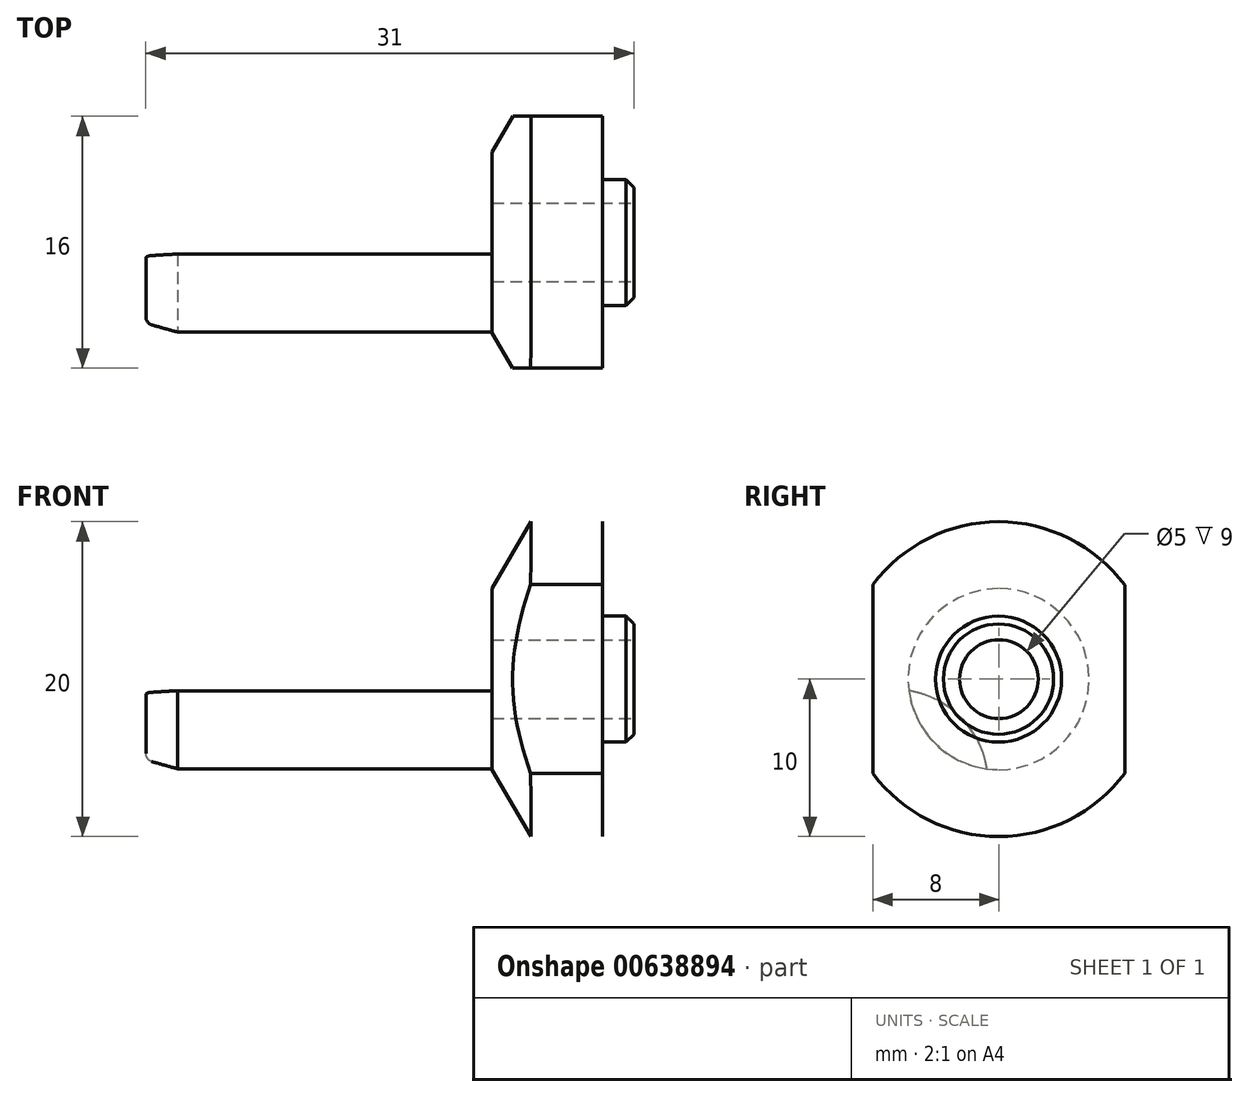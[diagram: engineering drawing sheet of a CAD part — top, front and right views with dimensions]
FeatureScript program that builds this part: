
annotation { "Feature Type Name" : "Feature", "Feature Type Description" : "" }
export const myFeature = defineFeature(function(context is Context, id is Id, definition is map)
    precondition{}
    {
        {
            var Q0;
            Q0=qCreatedBy(makeId("Top.planeOp"),FACE);
            var sketch = newSketch(context, id + "F0", { "sketchPlane" : qUnion([Q0])});
            skEllipticalArc(sketch, "E0", {});
            skEllipticalArc(sketch, "E1", {});
            skLineSegment(sketch, "E2", {"start": v(33.77, -5.77) * mm, "end": v(33.77, 5.73) * mm});
            skLineSegment(sketch, "E3", {"start": v(13.77, 5.73) * mm, "end": v(33.77, 5.73) * mm});
            skLineSegment(sketch, "E4", {"start": v(33.77, 5.68) * mm, "end": v(13.59, 5.68) * mm});
            skLineSegment(sketch, "E5", {"start": v(13.77, -5.77) * mm, "end": v(33.77, -5.77) * mm});
            skLineSegment(sketch, "E6", {"start": v(33.77, -5.72) * mm, "end": v(13.59, -5.72) * mm});
            skLineSegment(sketch, "E7", {"start": v(33.77, 0.73) * mm, "end": v(13.77, 0.73) * mm});
            skLineSegment(sketch, "E8", {"start": v(33.77, -0.77) * mm, "end": v(13.77, -0.77) * mm});
            skLineSegment(sketch, "E9", {"start": v(42.27, 3.98) * mm, "end": v(42.27, -4.02) * mm});
            skLineSegment(sketch, "E10", {"start": v(42.77, 3.48) * mm, "end": v(42.27, 3.98) * mm});
            skLineSegment(sketch, "E11", {"start": v(42.27, -4.02) * mm, "end": v(42.77, -3.52) * mm});
            skLineSegment(sketch, "E12", {"start": v(40.77, 5.98) * mm, "end": v(36.23, -6.02) * mm});
            skLineSegment(sketch, "E13", {"start": v(40.77, -6.02) * mm, "end": v(36.23, 5.98) * mm});
            skLineSegment(sketch, "E14", {"start": v(36.23, 9.98) * mm, "end": v(36.23, 5.98) * mm});
            skLineSegment(sketch, "E15", {"start": v(36.23, -6.02) * mm, "end": v(36.23, -10.02) * mm});
            skEllipticalArc(sketch, "E16", {});
            skLineSegment(sketch, "E17", {"start": v(40.77, -6.02) * mm, "end": v(36.23, -6.02) * mm});
            skLineSegment(sketch, "E18", {"start": v(40.77, 5.98) * mm, "end": v(36.23, 5.98) * mm});
            skLineSegment(sketch, "E19", {"start": v(42.77, 3.48) * mm, "end": v(42.77, -3.52) * mm});
            skLineSegment(sketch, "E20", {"start": v(42.77, 2.05) * mm, "end": v(30.27, 2.05) * mm});
            skLineSegment(sketch, "E21", {"start": v(30.27, 2.05) * mm, "end": v(30.27, -2.08) * mm});
            skLineSegment(sketch, "E22", {"start": v(30.27, -2.08) * mm, "end": v(42.77, -2.08) * mm});
            skLineSegment(sketch, "E23", {"start": v(30.27, -2.08) * mm, "end": v(29.08, -0.02) * mm});
            skLineSegment(sketch, "E24", {"start": v(30.27, 2.05) * mm, "end": v(29.08, -0.02) * mm});
            skLineSegment(sketch, "E25", {"start": v(32.77, 2.48) * mm, "end": v(32.77, -2.52) * mm});
            skLineSegment(sketch, "E26", {"start": v(32.77, -2.52) * mm, "end": v(42.77, -2.52) * mm});
            skLineSegment(sketch, "E27", {"start": v(42.77, 2.48) * mm, "end": v(32.77, 2.48) * mm});
            skLineSegment(sketch, "E28", {"start": v(32.77, -2.52) * mm, "end": v(32.02, -2.08) * mm});
            skLineSegment(sketch, "E29", {"start": v(32.77, 2.48) * mm, "end": v(32.02, 2.05) * mm});
            skLineSegment(sketch, "E30", {"start": v(27.71, -0.02) * mm, "end": v(44.14, -0.02) * mm});
            skLineSegment(sketch, "E31", {"start": v(42.27, 3.98) * mm, "end": v(40.77, 3.98) * mm});
            skLineSegment(sketch, "E32", {"start": v(42.27, -4.02) * mm, "end": v(40.77, -4.02) * mm});
            skLineSegment(sketch, "E33", {"start": v(33.77, -5.77) * mm, "end": v(36.23, -10.02) * mm});
            skLineSegment(sketch, "E34", {"start": v(33.77, 5.73) * mm, "end": v(36.23, 9.98) * mm});
            skLineSegment(sketch, "E35", {"start": v(40.77, -10.02) * mm, "end": v(40.77, 9.98) * mm});
            skLineSegment(sketch, "E36", {"start": v(40.77, -10.02) * mm, "end": v(36.23, -10.02) * mm});
            skLineSegment(sketch, "E37", {"start": v(40.77, 9.98) * mm, "end": v(36.23, 9.98) * mm});
            skLineSegment(sketch, "E38", {"start": v(6.87, -0.02) * mm, "end": v(34.27, -0.02) * mm});
            skLineSegment(sketch, "E39", {"start": v(13.77, -0.77) * mm, "end": v(13.77, 0.73) * mm});
            skLineSegment(sketch, "E40", {"start": v(12.14, -5.33) * mm, "end": v(13.77, -5.77) * mm});
            skLineSegment(sketch, "E41", {"start": v(11.77, 4.81) * mm, "end": v(11.77, -4.85) * mm});
            skLineSegment(sketch, "E42", {"start": v(12.14, 5.3) * mm, "end": v(13.77, 5.73) * mm});
            skArc(sketch, "E43", {"start": v(11.77, -4.85) * mm, "mid": v(11.88, -5.15) * mm, "end": v(12.14, -5.33) * mm});
            skArc(sketch, "E44", {"start": v(12.14, 5.3) * mm, "mid": v(11.88, 5.12) * mm, "end": v(11.77, 4.81) * mm});
            skArc(sketch, "E45", {"start": v(-24.14, 5.98) * mm, "mid": v(-32.14, 9.98) * mm, "end": v(-40.14, 5.98) * mm});
            skArc(sketch, "E46", {"start": v(-40.14, -6.02) * mm, "mid": v(-32.14, -10.02) * mm, "end": v(-24.14, -6.02) * mm});
            skLineSegment(sketch, "E47", {"start": v(-40.14, 5.98) * mm, "end": v(-40.14, -6.02) * mm});
            skLineSegment(sketch, "E48", {"start": v(-24.14, 5.98) * mm, "end": v(-24.14, -6.02) * mm});
            skCircle(sketch, "E49", {"center": v(-32.14, -0.02) * mm, "radius": 5.75 * mm});
            skLineSegment(sketch, "E50", {"start": v(-33.4, -4.11) * mm, "end": v(-32.14, -2.86) * mm});
            skLineSegment(sketch, "E51", {"start": v(-33.64, -3.65) * mm, "end": v(-32.14, -2.15) * mm});
            skLineSegment(sketch, "E52", {"start": v(-33.92, -3.22) * mm, "end": v(-32.14, -1.44) * mm});
            skLineSegment(sketch, "E53", {"start": v(-34.23, -2.82) * mm, "end": v(-32.14, -0.74) * mm});
            skLineSegment(sketch, "E54", {"start": v(-34.57, -2.45) * mm, "end": v(-32.14, -0.03) * mm});
            skLineSegment(sketch, "E55", {"start": v(-34.93, -2.11) * mm, "end": v(-32.84, -0.02) * mm});
            skLineSegment(sketch, "E56", {"start": v(-35.33, -1.8) * mm, "end": v(-33.55, -0.02) * mm});
            skLineSegment(sketch, "E57", {"start": v(-35.76, -1.53) * mm, "end": v(-34.25, -0.02) * mm});
            skLineSegment(sketch, "E58", {"start": v(-36.22, -1.28) * mm, "end": v(-34.96, -0.02) * mm});
            skLineSegment(sketch, "E59", {"start": v(-36.72, -1.07) * mm, "end": v(-35.67, -0.02) * mm});
            skLineSegment(sketch, "E60", {"start": v(-37.25, -0.9) * mm, "end": v(-36.37, -0.02) * mm});
            skLineSegment(sketch, "E61", {"start": v(-37.83, -0.77) * mm, "end": v(-37.08, -0.02) * mm});
            skLineSegment(sketch, "E62", {"start": v(-37.9, -0.12) * mm, "end": v(-37.79, -0.02) * mm});
            skLineSegment(sketch, "E63", {"start": v(-26.48, -0.02) * mm, "end": v(-26.4, 0.06) * mm});
            skLineSegment(sketch, "E64", {"start": v(-27.18, -0.02) * mm, "end": v(-26.44, 0.72) * mm});
            skLineSegment(sketch, "E65", {"start": v(-27.89, -0.02) * mm, "end": v(-27.02, 0.85) * mm});
            skLineSegment(sketch, "E66", {"start": v(-28.6, -0.02) * mm, "end": v(-27.55, 1.02) * mm});
            skLineSegment(sketch, "E67", {"start": v(-29.3, -0.02) * mm, "end": v(-28.05, 1.23) * mm});
            skLineSegment(sketch, "E68", {"start": v(-30.01, -0.02) * mm, "end": v(-28.51, 1.48) * mm});
            skLineSegment(sketch, "E69", {"start": v(-30.72, -0.02) * mm, "end": v(-28.94, 1.76) * mm});
            skLineSegment(sketch, "E70", {"start": v(-31.43, -0.02) * mm, "end": v(-29.34, 2.07) * mm});
            skLineSegment(sketch, "E71", {"start": v(-32.13, -0.02) * mm, "end": v(-29.7, 2.4) * mm});
            skLineSegment(sketch, "E72", {"start": v(-32.14, 0.68) * mm, "end": v(-30.05, 2.77) * mm});
            skLineSegment(sketch, "E73", {"start": v(-32.14, 1.38) * mm, "end": v(-30.36, 3.17) * mm});
            skLineSegment(sketch, "E74", {"start": v(-32.14, 2.1) * mm, "end": v(-30.64, 3.6) * mm});
            skLineSegment(sketch, "E75", {"start": v(-32.14, 2.8) * mm, "end": v(-30.88, 4.06) * mm});
            skArc(sketch, "E76", {"start": v(-31.4, 5.68) * mm, "mid": v(-29.71, 2.4) * mm, "end": v(-26.44, 0.73) * mm});
            skArc(sketch, "E77", {"start": v(-37.84, 0.73) * mm, "mid": v(-34.57, 2.4) * mm, "end": v(-32.9, 5.68) * mm});
            skArc(sketch, "E78", {"start": v(-32.9, -5.72) * mm, "mid": v(-34.57, -2.45) * mm, "end": v(-37.84, -0.77) * mm});
            skArc(sketch, "E79", {"start": v(-26.44, -0.77) * mm, "mid": v(-29.71, -2.45) * mm, "end": v(-31.4, -5.72) * mm});
            skPoint(sketch, "E80", {"position": v(11.77, -0.02) * mm});
            const initialGuessF0  = {"E0": [0.013773095000000013, 0.0011623069999999985, 0, -5, 0.005, 0.000431623, 4.300845, 4.712389], "E1": [0.013773095000000013, -0.001200938000000008, 0, 5, 0.005, 0.000431623, 4.712389, 5.123933], "E16": [0.036226833, -1.9316000000003442e-05, -6, 0, 0.006, 0.001154701, 3.141593, 6.283185]};
            skSetInitialGuess(sketch, initialGuessF0);
            skSolve(sketch);
        }
        {
            var Q0;
            {var subQ0=sQuery(id+"F0.wireOp",EDGE,"E31");Q0=makeQuery(id+"F0.imprint","IMPRINT",FACE,{"disambiguationData":[TD([[makeQuery(id+"F0.imprint","IMPRINT",EDGE,{"derivedFrom":subQ0}),1.0]])]});}
            var Q1;
            {var subQ0=sQuery(id+"F0.wireOp",EDGE,"E14");Q1=makeQuery(id+"F0.imprint","IMPRINT",FACE,{"disambiguationData":[TD([[makeQuery(id+"F0.imprint","IMPRINT",EDGE,{"derivedFrom":subQ0}),-1.0]])]});}
            var Q2;
            {var subQ0=sQuery(id+"F0.wireOp",EDGE,"E18");Q2=makeQuery(id+"F0.imprint","IMPRINT",FACE,{"disambiguationData":[TD([[makeQuery(id+"F0.imprint","IMPRINT",EDGE,{"derivedFrom":subQ0}),1.0]])]});}
            var Q3;
            {var subQ0=sQuery(id+"F0.wireOp",EDGE,"E27");var subQ1=sQuery(id+"F0.wireOp",EDGE,"E9");var subQ2=makeQuery(id+"F0.imprint","INTERSECT",VERTEX,{"derivedFrom":[subQ1,subQ0]});Q3=makeQuery(id+"F0.imprint","IMPRINT",FACE,{"disambiguationData":[TD([[makeQuery(id+"F0.imprint","IMPRINT",EDGE,{"disambiguationData":[TD([[subQ2,-1.0]])],"derivedFrom":subQ1}),1.0]])]});}
            var Q4;
            {var subQ1=sQuery(id+"F0.wireOp",EDGE,"E12");var subQ3=sQuery(id+"F0.wireOp",EDGE,"E27");var subQ4=makeQuery(id+"F0.imprint","INTERSECT",VERTEX,{"derivedFrom":[subQ1,subQ3]});Q4=makeQuery(id+"F0.imprint","IMPRINT",FACE,{"disambiguationData":[TD([[makeQuery(id+"F0.imprint","IMPRINT",EDGE,{"disambiguationData":[TD([[subQ4,1.0]])],"derivedFrom":subQ3}),-1.0]])]});}
            var Q5;
            {var subQ0=sQuery(id+"F0.wireOp",EDGE,"E27");var subQ1=sQuery(id+"F0.wireOp",EDGE,"E9");var subQ2=makeQuery(id+"F0.imprint","INTERSECT",VERTEX,{"derivedFrom":[subQ1,subQ0]});Q5=makeQuery(id+"F0.imprint","IMPRINT",FACE,{"disambiguationData":[TD([[makeQuery(id+"F0.imprint","IMPRINT",EDGE,{"disambiguationData":[TD([[subQ2,-1.0]])],"derivedFrom":subQ1}),-1.0]])]});}
            var Q6;
            {var subQ0=sQuery(id+"F0.wireOp",EDGE,"E10");Q6=makeQuery(id+"F0.imprint","IMPRINT",FACE,{"disambiguationData":[TD([[makeQuery(id+"F0.imprint","IMPRINT",EDGE,{"derivedFrom":subQ0}),1.0]])]});}
            var Q7;
            Q7=makeQuery(id+"F0.imprint","IMPRINT",FACE,{"disambiguationData":[TD([[makeQuery(id+"F0.imprint","IMPRINT",EDGE,{"derivedFrom":sQuery(id+"F0.wireOp",EDGE,"E14")}),1.0]])]});
            var Q8;
            {var subQ0=sQuery(id+"F0.wireOp",EDGE,"E20");var subQ1=sQuery(id+"F0.wireOp",EDGE,"E9");var subQ2=makeQuery(id+"F0.imprint","INTERSECT",VERTEX,{"derivedFrom":[subQ1,subQ0]});Q8=makeQuery(id+"F0.imprint","IMPRINT",FACE,{"disambiguationData":[TD([[makeQuery(id+"F0.imprint","IMPRINT",EDGE,{"disambiguationData":[TD([[subQ2,-1.0]])],"derivedFrom":subQ1}),-1.0]])]});}
            var Q9;
            {var subQ0=sQuery(id+"F0.wireOp",EDGE,"E20");var subQ1=sQuery(id+"F0.wireOp",EDGE,"E9");var subQ2=makeQuery(id+"F0.imprint","INTERSECT",VERTEX,{"derivedFrom":[subQ1,subQ0]});Q9=makeQuery(id+"F0.imprint","IMPRINT",FACE,{"disambiguationData":[TD([[makeQuery(id+"F0.imprint","IMPRINT",EDGE,{"disambiguationData":[TD([[subQ2,-1.0]])],"derivedFrom":subQ1}),1.0]])]});}
            var Q10;
            {var subQ0=sQuery(id+"F0.wireOp",EDGE,"E27");var subQ1=sQuery(id+"F0.wireOp",EDGE,"E12");var subQ2=makeQuery(id+"F0.imprint","INTERSECT",VERTEX,{"derivedFrom":[subQ1,subQ0]});Q10=makeQuery(id+"F0.imprint","IMPRINT",FACE,{"disambiguationData":[TD([[makeQuery(id+"F0.imprint","IMPRINT",EDGE,{"disambiguationData":[TD([[subQ2,-1.0]])],"derivedFrom":subQ1}),1.0]])]});}
            var Q11;
            {var subQ1=sQuery(id+"F0.wireOp",EDGE,"E2");var subQ7=makeQuery(id+"F0.imprint","INTERSECT",VERTEX,{"derivedFrom":[subQ1,sQuery(id+"F0.wireOp",EDGE,"E7")]});Q11=makeQuery(id+"F0.imprint","IMPRINT",FACE,{"disambiguationData":[TD([[makeQuery(id+"F0.imprint","IMPRINT",EDGE,{"disambiguationData":[TD([[subQ7,1.0]])],"derivedFrom":subQ1}),-1.0]])]});}
            var Q12;
            {var subQ0=sQuery(id+"F0.wireOp",EDGE,"E16");var subQ1=sQuery(id+"F0.wireOp",EDGE,"E2");var subQ2=makeQuery(id+"F0.imprint","INTERSECT",VERTEX,{"derivedFrom":[subQ1,subQ0]});Q12=makeQuery(id+"F0.imprint","IMPRINT",FACE,{"disambiguationData":[TD([[makeQuery(id+"F0.imprint","IMPRINT",EDGE,{"disambiguationData":[TD([[subQ2,-1.0]])],"derivedFrom":subQ1}),-1.0]])]});}
            var Q13;
            {var subQ0=sQuery(id+"F0.wireOp",EDGE,"E20");var subQ1=sQuery(id+"F0.wireOp",EDGE,"E2");var subQ2=makeQuery(id+"F0.imprint","INTERSECT",VERTEX,{"derivedFrom":[subQ1,subQ0]});Q13=makeQuery(id+"F0.imprint","IMPRINT",FACE,{"disambiguationData":[TD([[makeQuery(id+"F0.imprint","IMPRINT",EDGE,{"disambiguationData":[TD([[subQ2,-1.0]])],"derivedFrom":subQ1}),-1.0]])]});}
            var Q14;
            {var subQ0=sQuery(id+"F0.wireOp",EDGE,"E20");var subQ1=sQuery(id+"F0.wireOp",EDGE,"E12");var subQ2=makeQuery(id+"F0.imprint","INTERSECT",VERTEX,{"derivedFrom":[subQ1,subQ0]});Q14=makeQuery(id+"F0.imprint","IMPRINT",FACE,{"disambiguationData":[TD([[makeQuery(id+"F0.imprint","IMPRINT",EDGE,{"disambiguationData":[TD([[subQ2,-1.0]])],"derivedFrom":subQ1}),-1.0]])]});}
            var Q15;
            {var subQ0=sQuery(id+"F0.wireOp",EDGE,"E16");var subQ1=sQuery(id+"F0.wireOp",EDGE,"E12");var subQ2=makeQuery(id+"F0.imprint","INTERSECT",VERTEX,{"derivedFrom":[subQ1,subQ0]});Q15=makeQuery(id+"F0.imprint","IMPRINT",FACE,{"disambiguationData":[TD([[makeQuery(id+"F0.imprint","IMPRINT",EDGE,{"disambiguationData":[TD([[subQ2,-1.0]])],"derivedFrom":subQ0}),1.0]])]});}
            var Q16;
            {var subQ0=sQuery(id+"F0.wireOp",EDGE,"E16");var subQ1=sQuery(id+"F0.wireOp",EDGE,"E12");var subQ2=makeQuery(id+"F0.imprint","INTERSECT",VERTEX,{"derivedFrom":[subQ1,subQ0]});Q16=makeQuery(id+"F0.imprint","IMPRINT",FACE,{"disambiguationData":[TD([[makeQuery(id+"F0.imprint","IMPRINT",EDGE,{"disambiguationData":[TD([[subQ2,1.0]])],"derivedFrom":subQ0}),1.0]])]});}
            var Q17;
            {var subQ0=sQuery(id+"F0.wireOp",EDGE,"E27");var subQ1=sQuery(id+"F0.wireOp",EDGE,"E12");var subQ2=makeQuery(id+"F0.imprint","INTERSECT",VERTEX,{"derivedFrom":[subQ1,subQ0]});Q17=makeQuery(id+"F0.imprint","IMPRINT",FACE,{"disambiguationData":[TD([[makeQuery(id+"F0.imprint","IMPRINT",EDGE,{"disambiguationData":[TD([[subQ2,-1.0]])],"derivedFrom":subQ1}),-1.0]])]});}
            var Q18;
            {var subQ0=sQuery(id+"F0.wireOp",EDGE,"E20");var subQ1=sQuery(id+"F0.wireOp",EDGE,"E12");var subQ2=makeQuery(id+"F0.imprint","INTERSECT",VERTEX,{"derivedFrom":[subQ1,subQ0]});Q18=makeQuery(id+"F0.imprint","IMPRINT",FACE,{"disambiguationData":[TD([[makeQuery(id+"F0.imprint","IMPRINT",EDGE,{"disambiguationData":[TD([[subQ2,-1.0]])],"derivedFrom":subQ1}),1.0]])]});}
            var Q19;
            {var subQ0=sQuery(id+"F0.wireOp",EDGE,"E30");var subQ1=sQuery(id+"F0.wireOp",EDGE,"E16");var subQ2=makeQuery(id+"F0.imprint","INTERSECT",VERTEX,{"derivedFrom":[subQ1,subQ0]});Q19=makeQuery(id+"F0.imprint","IMPRINT",FACE,{"disambiguationData":[TD([[makeQuery(id+"F0.imprint","IMPRINT",EDGE,{"disambiguationData":[TD([[subQ2,-1.0]])],"derivedFrom":subQ1}),1.0]])]});}
            var Q20;
            Q20=sQuery(id+"F0.wireOp",EDGE,"E38");
            revolve(context, id + "F1", {"entities" : qUnion([Q0, Q1, Q2, Q3, Q4, Q5, Q6, Q7, Q8, Q9, Q10, Q11, Q12, Q13, Q14, Q15, Q16, Q17, Q18, Q19]), "axis" : qUnion([Q20]), "revolveType" : RevolveType.FULL});
        }
        {
            var Q0;
            Q0=makeQuery(id+"F1.opRevolve","SWEPT_FACE",FACE,{"disambiguationData":[OSD([sQuery(id+"F0.wireOp",EDGE,"E35")])]});
            var sketch = newSketch(context, id + "F2", { "sketchPlane" : qUnion([Q0])});
            skArc(sketch, "E81", {"start": v(6, -7.99) * mm, "mid": v(10, 0.01) * mm, "end": v(6, 8.01) * mm});
            skArc(sketch, "E82", {"start": v(-6, 8.01) * mm, "mid": v(-10, 0.01) * mm, "end": v(-6, -7.99) * mm});
            skLineSegment(sketch, "E83", {"start": v(6, 8.01) * mm, "end": v(-6, 8.01) * mm});
            skLineSegment(sketch, "E84", {"start": v(6, -7.99) * mm, "end": v(-6, -7.99) * mm});
            skCircle(sketch, "E85", {"center": v(0, 0.01) * mm, "radius": 5.75 * mm});
            skLineSegment(sketch, "E86", {"start": v(-4.1, 1.26) * mm, "end": v(-2.84, 0.01) * mm});
            skLineSegment(sketch, "E87", {"start": v(-3.63, 1.5) * mm, "end": v(-2.13, 0.01) * mm});
            skLineSegment(sketch, "E88", {"start": v(-3.2, 1.79) * mm, "end": v(-1.42, 0.01) * mm});
            skLineSegment(sketch, "E89", {"start": v(-2.8, 2.1) * mm, "end": v(-0.72, 0.01) * mm});
            skLineSegment(sketch, "E90", {"start": v(-2.43, 2.43) * mm, "end": v(-0.01, 0.01) * mm});
            skLineSegment(sketch, "E91", {"start": v(-2.1, 2.8) * mm, "end": v(0, 0.7) * mm});
            skLineSegment(sketch, "E92", {"start": v(-1.78, 3.2) * mm, "end": v(0, 1.41) * mm});
            skLineSegment(sketch, "E93", {"start": v(-1.5, 3.63) * mm, "end": v(0, 2.12) * mm});
            skLineSegment(sketch, "E94", {"start": v(-1.26, 4.09) * mm, "end": v(0, 2.83) * mm});
            skLineSegment(sketch, "E95", {"start": v(-1.05, 4.58) * mm, "end": v(0, 3.54) * mm});
            skLineSegment(sketch, "E96", {"start": v(-0.88, 5.12) * mm, "end": v(0, 4.24) * mm});
            skLineSegment(sketch, "E97", {"start": v(-0.75, 5.7) * mm, "end": v(0, 4.95) * mm});
            skLineSegment(sketch, "E98", {"start": v(-0.1, 5.76) * mm, "end": v(0, 5.66) * mm});
            skLineSegment(sketch, "E99", {"start": v(0, -5.66) * mm, "end": v(0.08, -5.74) * mm});
            skLineSegment(sketch, "E100", {"start": v(0, -4.95) * mm, "end": v(0.74, -5.7) * mm});
            skLineSegment(sketch, "E101", {"start": v(0, -4.24) * mm, "end": v(0.87, -5.12) * mm});
            skLineSegment(sketch, "E102", {"start": v(0, -3.54) * mm, "end": v(1.04, -4.58) * mm});
            skLineSegment(sketch, "E103", {"start": v(0, -2.83) * mm, "end": v(1.25, -4.08) * mm});
            skLineSegment(sketch, "E104", {"start": v(0, -2.12) * mm, "end": v(1.5, -3.62) * mm});
            skLineSegment(sketch, "E105", {"start": v(0, -1.41) * mm, "end": v(1.78, -3.2) * mm});
            skLineSegment(sketch, "E106", {"start": v(0, -0.7) * mm, "end": v(2.09, -2.8) * mm});
            skLineSegment(sketch, "E107", {"start": v(0, 0) * mm, "end": v(2.42, -2.42) * mm});
            skLineSegment(sketch, "E108", {"start": v(0.7, 0.01) * mm, "end": v(2.8, -2.08) * mm});
            skLineSegment(sketch, "E109", {"start": v(1.4, 0.01) * mm, "end": v(3.19, -1.77) * mm});
            skLineSegment(sketch, "E110", {"start": v(2.11, 0.01) * mm, "end": v(3.62, -1.5) * mm});
            skLineSegment(sketch, "E111", {"start": v(2.82, 0.01) * mm, "end": v(4.08, -1.25) * mm});
            skArc(sketch, "E112", {"start": v(5.7, -0.74) * mm, "mid": v(2.43, -2.42) * mm, "end": v(0.75, -5.7) * mm});
            skArc(sketch, "E113", {"start": v(0.75, 5.71) * mm, "mid": v(2.43, 2.44) * mm, "end": v(5.7, 0.76) * mm});
            skArc(sketch, "E114", {"start": v(-5.7, 0.76) * mm, "mid": v(-2.43, 2.44) * mm, "end": v(-0.75, 5.71) * mm});
            skArc(sketch, "E115", {"start": v(-0.75, -5.7) * mm, "mid": v(-2.43, -2.42) * mm, "end": v(-5.7, -0.74) * mm});
            skSolve(sketch);
        }
        {
            var Q0;
            Q0=makeQuery(id+"F1.opRevolve","SWEPT_FACE",FACE,{"disambiguationData":[OSD([sQuery(id+"F0.wireOp",EDGE,"E2")])]});
            var sketch = newSketch(context, id + "F3", { "sketchPlane" : qUnion([Q0])});
            skPoint(sketch, "E116.0", {"position": v(0.02, 0) * mm});
            skArc(sketch, "E117.0", {"start": v(-0.75, 5.71) * mm, "mid": v(-2.43, 2.44) * mm, "end": v(-5.7, 0.76) * mm});
            skArc(sketch, "E117.1", {"start": v(5.7, 0.76) * mm, "mid": v(2.43, 2.44) * mm, "end": v(0.75, 5.71) * mm});
            skCircle(sketch, "E117.2", {"center": v(0, 0.01) * mm, "radius": 5.75 * mm});
            skArc(sketch, "E117.3", {"start": v(0.75, -5.7) * mm, "mid": v(2.43, -2.42) * mm, "end": v(5.7, -0.74) * mm});
            skArc(sketch, "E117.4", {"start": v(-5.7, -0.74) * mm, "mid": v(-2.43, -2.42) * mm, "end": v(-0.75, -5.7) * mm});
            skSolve(sketch);
        }
        {
            var Q0;
            {var subQ3=sQuery(id+"F3.wireOp",EDGE,"E117.3");Q0=makeQuery(id+"F3.imprint","IMPRINT",FACE,{"disambiguationData":[TD([[makeQuery(id+"F3.imprint","IMPRINT",EDGE,{"derivedFrom":subQ3}),1.0]])]});}
            extrude(context, id + "F4", {"entities" : qUnion([Q0]), "operationType" : NewBodyOperationType.ADD, "depth" : 22 * mm, "offsetDistance" : 25 * mm});
        }
        {
            var Q0;
            {var subQ0=sQuery(id+"F0.wireOp",EDGE,"E34");var subQ1=sQuery(id+"F0.wireOp",EDGE,"E3");var subQ2=sQuery(id+"F0.wireOp",EDGE,"E2");var subQ3=makeQuery(id+"F1.opRevolve","SWEPT_EDGE",EDGE,{"disambiguationData":[OSD([subQ2,subQ1,subQ0])]});Q0=makeQuery(id+"F4.opExtrude","CAP_EDGE",EDGE,{"disambiguationData":[OSD([subQ2,subQ1,subQ0]),TDD([makeQuery(id+"F3.imprint","IMPRINT",EDGE,{"disambiguationData":[TD([[makeQuery(id+"F3.imprint","INTERSECT",VERTEX,{"disambiguationData":[OD(0.0)],"derivedFrom":[subQ3,sQuery(id+"F3.wireOp",EDGE,"E117.0")]}),1.0]])],"derivedFrom":subQ3})])],"isStart":false});}
            var Q1;
            {var subQ0=sQuery(id+"F3.wireOp",EDGE,"E117.2");Q1=makeQuery(id+"F4.opExtrude","CAP_EDGE",EDGE,{"disambiguationData":[OSD([subQ0]),TDD([makeQuery(id+"F3.imprint","IMPRINT",EDGE,{"disambiguationData":[TD([[makeQuery(id+"F3.imprint","INTERSECT",VERTEX,{"disambiguationData":[OD(0.0)],"derivedFrom":[sQuery(id+"F3.wireOp",EDGE,"E117.1"),subQ0]}),1.0]])],"derivedFrom":subQ0})])],"isStart":false});}
            var Q2;
            {var subQ0=sQuery(id+"F3.wireOp",EDGE,"E117.2");Q2=makeQuery(id+"F4.opExtrude","CAP_EDGE",EDGE,{"disambiguationData":[OSD([subQ0]),TDD([makeQuery(id+"F3.imprint","IMPRINT",EDGE,{"disambiguationData":[TD([[makeQuery(id+"F3.imprint","INTERSECT",VERTEX,{"disambiguationData":[OD(0.0)],"derivedFrom":[subQ0,sQuery(id+"F3.wireOp",EDGE,"E117.3")]}),1.0]])],"derivedFrom":subQ0})])],"isStart":false});}
            var Q3;
            {var subQ0=sQuery(id+"F0.wireOp",EDGE,"E34");var subQ1=sQuery(id+"F0.wireOp",EDGE,"E3");var subQ2=sQuery(id+"F0.wireOp",EDGE,"E2");var subQ3=makeQuery(id+"F1.opRevolve","SWEPT_EDGE",EDGE,{"disambiguationData":[OSD([subQ2,subQ1,subQ0])]});Q3=makeQuery(id+"F4.opExtrude","CAP_EDGE",EDGE,{"disambiguationData":[OSD([subQ2,subQ1,subQ0]),TDD([makeQuery(id+"F3.imprint","IMPRINT",EDGE,{"disambiguationData":[TD([[makeQuery(id+"F3.imprint","INTERSECT",VERTEX,{"derivedFrom":[subQ3,sQuery(id+"F3.wireOp",EDGE,"E117.4")]}),1.0]])],"derivedFrom":subQ3})])],"isStart":false});}
            chamfer(context, id + "F5", {"entities" : qUnion([Q0, Q1, Q2, Q3]), "chamferType" : ChamferType.OFFSET_ANGLE, "width" : 2 * mm, "oppositeDirection" : true, "angle" : 15 * degree, "tangentPropagation" : true});
        }
        {
            var Q0;
            {var subQ0=sQuery(id+"F3.wireOp",EDGE,"E117.1");var subQ1=sQuery(id+"F3.wireOp",EDGE,"E117.0");var subQ2=sQuery(id+"F0.wireOp",EDGE,"E34");var subQ3=sQuery(id+"F0.wireOp",EDGE,"E3");var subQ4=sQuery(id+"F0.wireOp",EDGE,"E2");var subQ5=makeQuery(id+"F1.opRevolve","SWEPT_EDGE",EDGE,{"disambiguationData":[OSD([subQ4,subQ3,subQ2])]});Q0=makeQuery(id+"F5.opChamfer","BLEND_EDGE",EDGE,{"blendedFrom":[makeQuery(id+"F4.opExtrude","CAP_EDGE",EDGE,{"disambiguationData":[OSD([subQ4,subQ3,subQ2]),TDD([makeQuery(id+"F3.imprint","IMPRINT",EDGE,{"disambiguationData":[TD([[makeQuery(id+"F3.imprint","INTERSECT",VERTEX,{"disambiguationData":[OD(0.0)],"derivedFrom":[subQ5,subQ1]}),1.0]])],"derivedFrom":subQ5})])],"isStart":false}),makeQuery(id+"F4.opExtrude","CAP_FACE",FACE,{"disambiguationData":[OSD([subQ4,subQ3,subQ2,subQ1,subQ0,sQuery(id+"F3.wireOp",EDGE,"E117.2"),sQuery(id+"F3.wireOp",EDGE,"E117.3"),sQuery(id+"F3.wireOp",EDGE,"E117.4")])],"isStart":false})],"blendedInto":[makeQuery(id+"F4.opExtrude","CAP_FACE",FACE,{"disambiguationData":[OSD([subQ4,subQ3,subQ2,subQ1,subQ0,sQuery(id+"F3.wireOp",EDGE,"E117.2"),sQuery(id+"F3.wireOp",EDGE,"E117.3"),sQuery(id+"F3.wireOp",EDGE,"E117.4")])],"isStart":false})]});}
            var Q1;
            {var subQ0=sQuery(id+"F3.wireOp",EDGE,"E117.4");var subQ1=sQuery(id+"F3.wireOp",EDGE,"E117.0");var subQ2=sQuery(id+"F0.wireOp",EDGE,"E34");var subQ3=sQuery(id+"F0.wireOp",EDGE,"E3");var subQ4=sQuery(id+"F0.wireOp",EDGE,"E2");var subQ5=makeQuery(id+"F1.opRevolve","SWEPT_EDGE",EDGE,{"disambiguationData":[OSD([subQ4,subQ3,subQ2])]});Q1=makeQuery(id+"F5.opChamfer","BLEND_EDGE",EDGE,{"blendedFrom":[makeQuery(id+"F4.opExtrude","CAP_EDGE",EDGE,{"disambiguationData":[OSD([subQ4,subQ3,subQ2]),TDD([makeQuery(id+"F3.imprint","IMPRINT",EDGE,{"disambiguationData":[TD([[makeQuery(id+"F3.imprint","INTERSECT",VERTEX,{"derivedFrom":[subQ5,subQ0]}),1.0]])],"derivedFrom":subQ5})])],"isStart":false}),makeQuery(id+"F4.opExtrude","CAP_FACE",FACE,{"disambiguationData":[OSD([subQ4,subQ3,subQ2,subQ1,sQuery(id+"F3.wireOp",EDGE,"E117.1"),sQuery(id+"F3.wireOp",EDGE,"E117.2"),sQuery(id+"F3.wireOp",EDGE,"E117.3"),subQ0])],"isStart":false})],"blendedInto":[makeQuery(id+"F4.opExtrude","CAP_FACE",FACE,{"disambiguationData":[OSD([subQ4,subQ3,subQ2,subQ1,sQuery(id+"F3.wireOp",EDGE,"E117.1"),sQuery(id+"F3.wireOp",EDGE,"E117.2"),sQuery(id+"F3.wireOp",EDGE,"E117.3"),subQ0])],"isStart":false})]});}
            var Q2;
            {var subQ0=sQuery(id+"F3.wireOp",EDGE,"E117.3");var subQ1=sQuery(id+"F3.wireOp",EDGE,"E117.2");var subQ2=sQuery(id+"F3.wireOp",EDGE,"E117.1");Q2=makeQuery(id+"F5.opChamfer","BLEND_EDGE",EDGE,{"blendedFrom":[makeQuery(id+"F4.opExtrude","CAP_EDGE",EDGE,{"disambiguationData":[OSD([subQ1]),TDD([makeQuery(id+"F3.imprint","IMPRINT",EDGE,{"disambiguationData":[TD([[makeQuery(id+"F3.imprint","INTERSECT",VERTEX,{"disambiguationData":[OD(0.0)],"derivedFrom":[subQ2,subQ1]}),1.0]])],"derivedFrom":subQ1})])],"isStart":false}),makeQuery(id+"F4.opExtrude","CAP_FACE",FACE,{"disambiguationData":[OSD([sQuery(id+"F0.wireOp",EDGE,"E2"),sQuery(id+"F0.wireOp",EDGE,"E3"),sQuery(id+"F0.wireOp",EDGE,"E34"),sQuery(id+"F3.wireOp",EDGE,"E117.0"),subQ2,subQ1,subQ0,sQuery(id+"F3.wireOp",EDGE,"E117.4")])],"isStart":false})],"blendedInto":[makeQuery(id+"F4.opExtrude","CAP_FACE",FACE,{"disambiguationData":[OSD([sQuery(id+"F0.wireOp",EDGE,"E2"),sQuery(id+"F0.wireOp",EDGE,"E3"),sQuery(id+"F0.wireOp",EDGE,"E34"),sQuery(id+"F3.wireOp",EDGE,"E117.0"),subQ2,subQ1,subQ0,sQuery(id+"F3.wireOp",EDGE,"E117.4")])],"isStart":false})]});}
            fillet(context, id + "F6", {"entities" : qUnion([Q0, Q1, Q2]), "radius" : 0.5 * mm, "tangentPropagation" : true, "allowEdgeOverflow" : false});
        }
        {
            var Q0;
            Q0=makeQuery(id+"F1.opRevolve","SWEPT_FACE",FACE,{"disambiguationData":[OSD([sQuery(id+"F0.wireOp",EDGE,"E19")])]});
            var sketch = newSketch(context, id + "F7", { "sketchPlane" : qUnion([Q0])});
            skPoint(sketch, "E118", {"position": v(0, 0) * mm});
            skSolve(sketch);
        }
        {
            var Q0;
            Q0=sQuery(id+"F7.wireOp",VERTEX,"E118");
            var Q1;
            Q1=makeQuery(id+"F1.opRevolve","SWEPT_BODY",BODY,{"disambiguationData":[OSD([sQuery(id+"F0.wireOp",EDGE,"E2"),sQuery(id+"F0.wireOp",EDGE,"E10"),sQuery(id+"F0.wireOp",EDGE,"E19"),sQuery(id+"F0.wireOp",EDGE,"E30"),sQuery(id+"F0.wireOp",EDGE,"E31"),sQuery(id+"F0.wireOp",EDGE,"E34"),sQuery(id+"F0.wireOp",EDGE,"E35"),sQuery(id+"F0.wireOp",EDGE,"E37"),sQuery(id+"F0.wireOp",EDGE,"E38")])]});
            hole(context, id + "F8", {"style" : HoleStyle.SIMPLE, "endStyle" : HoleEndStyle.BLIND, "holeDiameter" : 5 * mm, "majorDiameter" : 5 * mm, "holeDepth" : 10 * mm, "isTappedThrough" : true, "tappedDepth" : 12 * mm, "tapClearance" : 3, "locations" : qUnion([Q0]), "scope" : qUnion([Q1])});
        }
        {
            var Q0;
            Q0=makeQuery(id+"F4.opExtrude","CAP_FACE",FACE,{"disambiguationData":[OSD([sQuery(id+"F0.wireOp",EDGE,"E2"),sQuery(id+"F0.wireOp",EDGE,"E3"),sQuery(id+"F0.wireOp",EDGE,"E34"),sQuery(id+"F3.wireOp",EDGE,"E117.0"),sQuery(id+"F3.wireOp",EDGE,"E117.1"),sQuery(id+"F3.wireOp",EDGE,"E117.2"),sQuery(id+"F3.wireOp",EDGE,"E117.3"),sQuery(id+"F3.wireOp",EDGE,"E117.4")])],"isStart":false});
            var sketch = newSketch(context, id + "F9", { "sketchPlane" : qUnion([Q0])});
            skPoint(sketch, "E119", {"position": v(0, 0) * mm});
            skSolve(sketch);
        }
        {
            var Q0;
            Q0=sQuery(id+"F9.wireOp",VERTEX,"E119");
            var Q1;
            Q1=makeQuery(id+"F1.opRevolve","SWEPT_BODY",BODY,{"disambiguationData":[OSD([sQuery(id+"F0.wireOp",EDGE,"E2"),sQuery(id+"F0.wireOp",EDGE,"E10"),sQuery(id+"F0.wireOp",EDGE,"E19"),sQuery(id+"F0.wireOp",EDGE,"E30"),sQuery(id+"F0.wireOp",EDGE,"E31"),sQuery(id+"F0.wireOp",EDGE,"E34"),sQuery(id+"F0.wireOp",EDGE,"E35"),sQuery(id+"F0.wireOp",EDGE,"E37"),sQuery(id+"F0.wireOp",EDGE,"E38")])]});
            hole(context, id + "F10", {"style" : HoleStyle.SIMPLE, "endStyle" : HoleEndStyle.BLIND, "holeDiameter" : 4 * mm, "majorDiameter" : 5 * mm, "holeDepth" : 6 * mm, "isTappedThrough" : true, "tappedDepth" : 12 * mm, "tapClearance" : 3, "locations" : qUnion([Q0]), "scope" : qUnion([Q1])});
        }
        {
            var Q0;
            Q0=makeQuery(id+"F1.opRevolve","SWEPT_FACE",FACE,{"disambiguationData":[OSD([sQuery(id+"F0.wireOp",EDGE,"E35")])]});
            var sketch = newSketch(context, id + "F11", { "sketchPlane" : qUnion([Q0])});
            skCircle(sketch, "E120.0", {"center": v(-0.02, 0) * mm, "radius": 10 * mm});
            skPoint(sketch, "E121", {"position": v(0, 0) * mm});
            skArc(sketch, "E122", {"start": v(8, 6) * mm, "mid": v(0, 10) * mm, "end": v(-8, 6) * mm});
            skArc(sketch, "E123", {"start": v(-8, -6) * mm, "mid": v(0, -10) * mm, "end": v(8, -6) * mm});
            skLineSegment(sketch, "E124", {"start": v(-8, 6) * mm, "end": v(-8, -6) * mm});
            skLineSegment(sketch, "E125", {"start": v(8, 6) * mm, "end": v(8, -6) * mm});
            skCircle(sketch, "E126", {"center": v(0, 0) * mm, "radius": 5.75 * mm});
            skLineSegment(sketch, "E127", {"start": v(-1.25, -4.1) * mm, "end": v(0, -2.84) * mm});
            skLineSegment(sketch, "E128", {"start": v(-1.5, -3.63) * mm, "end": v(0, -2.13) * mm});
            skLineSegment(sketch, "E129", {"start": v(-1.78, -3.2) * mm, "end": v(0, -1.42) * mm});
            skLineSegment(sketch, "E130", {"start": v(-2.09, -2.8) * mm, "end": v(0, -0.72) * mm});
            skLineSegment(sketch, "E131", {"start": v(-2.42, -2.43) * mm, "end": v(0, -0.01) * mm});
            skLineSegment(sketch, "E132", {"start": v(-2.8, -2.1) * mm, "end": v(-0.7, 0) * mm});
            skLineSegment(sketch, "E133", {"start": v(-3.19, -1.78) * mm, "end": v(-1.4, 0) * mm});
            skLineSegment(sketch, "E134", {"start": v(-3.62, -1.5) * mm, "end": v(-2.11, 0) * mm});
            skLineSegment(sketch, "E135", {"start": v(-4.08, -1.26) * mm, "end": v(-2.82, 0) * mm});
            skLineSegment(sketch, "E136", {"start": v(-4.57, -1.05) * mm, "end": v(-3.53, 0) * mm});
            skLineSegment(sketch, "E137", {"start": v(-5.11, -0.88) * mm, "end": v(-4.23, 0) * mm});
            skLineSegment(sketch, "E138", {"start": v(-5.7, -0.75) * mm, "end": v(-4.94, 0) * mm});
            skLineSegment(sketch, "E139", {"start": v(-5.75, -0.1) * mm, "end": v(-5.65, 0) * mm});
            skLineSegment(sketch, "E140", {"start": v(5.67, 0) * mm, "end": v(5.75, 0.08) * mm});
            skLineSegment(sketch, "E141", {"start": v(4.96, 0) * mm, "end": v(5.7, 0.74) * mm});
            skLineSegment(sketch, "E142", {"start": v(4.25, 0) * mm, "end": v(5.13, 0.87) * mm});
            skLineSegment(sketch, "E143", {"start": v(3.55, 0) * mm, "end": v(4.59, 1.04) * mm});
            skLineSegment(sketch, "E144", {"start": v(2.84, 0) * mm, "end": v(4.1, 1.25) * mm});
            skLineSegment(sketch, "E145", {"start": v(2.13, 0) * mm, "end": v(3.63, 1.5) * mm});
            skLineSegment(sketch, "E146", {"start": v(1.42, 0) * mm, "end": v(3.2, 1.78) * mm});
            skLineSegment(sketch, "E147", {"start": v(0.72, 0) * mm, "end": v(2.8, 2.09) * mm});
            skLineSegment(sketch, "E148", {"start": v(0.01, 0) * mm, "end": v(2.43, 2.42) * mm});
            skLineSegment(sketch, "E149", {"start": v(0, 0.7) * mm, "end": v(2.1, 2.8) * mm});
            skLineSegment(sketch, "E150", {"start": v(0, 1.4) * mm, "end": v(1.78, 3.19) * mm});
            skLineSegment(sketch, "E151", {"start": v(0, 2.11) * mm, "end": v(1.5, 3.62) * mm});
            skLineSegment(sketch, "E152", {"start": v(0, 2.82) * mm, "end": v(1.26, 4.08) * mm});
            skArc(sketch, "E153", {"start": v(0.75, 5.7) * mm, "mid": v(2.43, 2.43) * mm, "end": v(5.7, 0.75) * mm});
            skArc(sketch, "E154", {"start": v(-5.7, 0.75) * mm, "mid": v(-2.43, 2.43) * mm, "end": v(-0.75, 5.7) * mm});
            skArc(sketch, "E155", {"start": v(-0.75, -5.7) * mm, "mid": v(-2.43, -2.43) * mm, "end": v(-5.7, -0.75) * mm});
            skArc(sketch, "E156", {"start": v(5.7, -0.75) * mm, "mid": v(2.43, -2.43) * mm, "end": v(0.75, -5.7) * mm});
            skSolve(sketch);
        }
        {
            var Q0;
            {var subQ0=sQuery(id+"F11.wireOp",EDGE,"E125");var subQ1=sQuery(id+"F11.wireOp",EDGE,"E120.0");var subQ2=makeQuery(id+"F11.imprint","INTERSECT",VERTEX,{"disambiguationData":[OD(0.0)],"derivedFrom":[subQ1,subQ0]});Q0=makeQuery(id+"F11.imprint","IMPRINT",FACE,{"disambiguationData":[TD([[makeQuery(id+"F11.imprint","IMPRINT",EDGE,{"disambiguationData":[TD([[subQ2,-1.0]])],"derivedFrom":subQ1}),-1.0]])]});}
            var Q1;
            {var subQ5=sQuery(id+"F11.wireOp",EDGE,"E124");Q1=makeQuery(id+"F11.imprint","IMPRINT",FACE,{"disambiguationData":[TD([[makeQuery(id+"F11.imprint","IMPRINT",EDGE,{"derivedFrom":subQ5}),-1.0]])]});}
            extrude(context, id + "F12", {"entities" : qUnion([Q0, Q1]), "operationType" : NewBodyOperationType.REMOVE, "oppositeDirection" : true, "depth" : 25 * mm, "offsetDistance" : 25 * mm});
        }
    });
